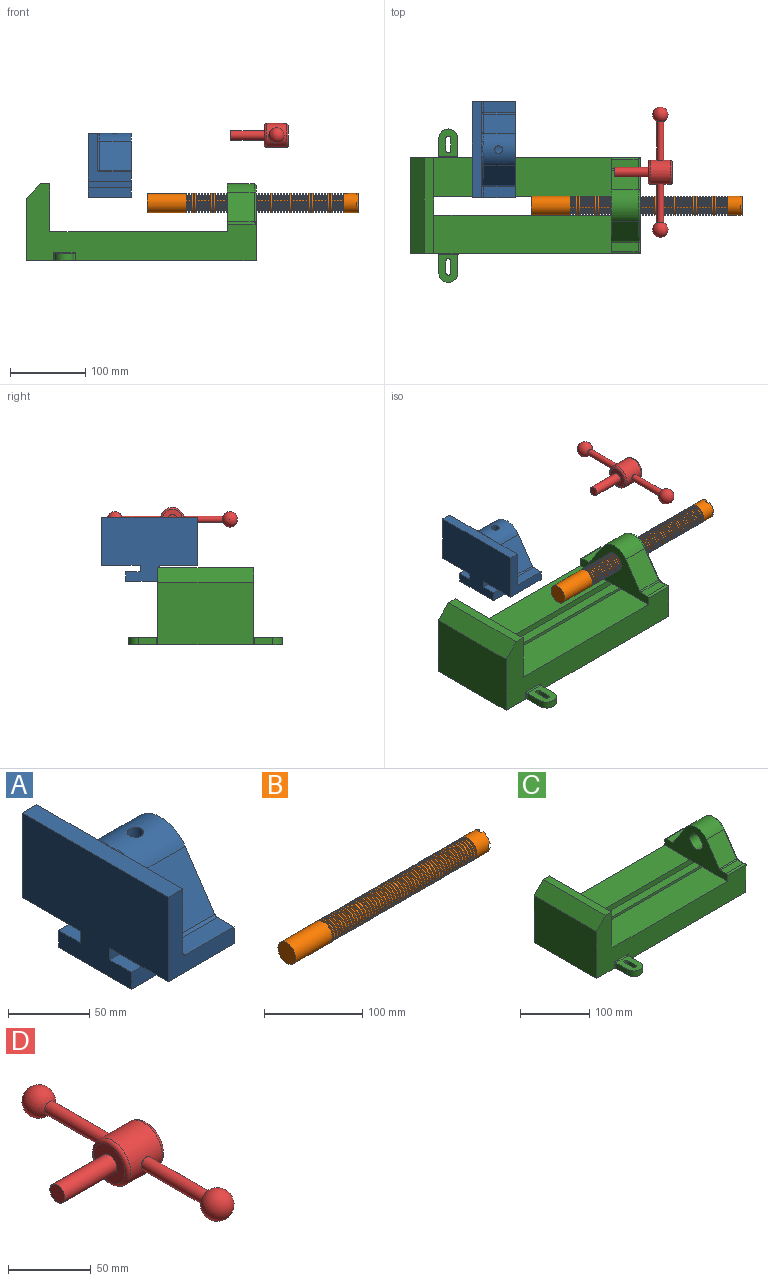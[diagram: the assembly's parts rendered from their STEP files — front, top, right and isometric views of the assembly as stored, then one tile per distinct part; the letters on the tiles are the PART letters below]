
ASSEMBLY  parts=4 mates=1
PART A: 36 faces, bbox 57.2x127x89 mm
  f0: plane 57.15x50.8mm, normal (0,0,-1), area 2903.2mm2, adj f6,f9,f10,f23
  f1: cylinder r=12.7mm len=44.45mm, axis (1,0,0), area 3464.3mm2, adj f6,f15,f16
  f2: plane 41.91x14.52mm, normal (0,0,1), area 608.5mm2, adj f6,f11,f24,f25
  f3: plane 51.86x48.26mm, normal (1,0,0), area 1495.7mm2, adj f8,f10,f31,f33,f35
  f4: plane 51.86x48.26mm, normal (1,0,0), area 1495.7mm2, adj f8,f11,f24,f28,f29
  f5: plane 57.15x50.8mm, normal (0,0,-1), area 2903.2mm2, adj f6,f9,f11,f22
  f6: plane 127x85.09mm, normal (1,0,0), area 5190.6mm2, adj f0,f1,f2,f5,f7,f10,f11,f12
  f7: plane 41.91x14.52mm, normal (0,0,1), area 608.5mm2, adj f6,f10,f30,f31
  f8: plane 127x12.7mm, normal (0,0,1), area 1612.9mm2, adj f3,f4,f9,f10,f11,f26,f34
  f9: plane 127x85.09mm, normal (-1,0,0), area 9096.8mm2, adj f0,f5,f8,f10,f11,f17,f18,f19
  f10: plane 63.5x57.15mm, normal (0,-1,0), area 1372.3mm2, adj f0,f3,f6,f7,f8,f9,f31
  f11: plane 63.5x57.15mm, normal (0,1,0), area 1372.3mm2, adj f2,f4,f5,f6,f8,f9,f24
  f12: plane 41.91x38.43mm, normal (0,-0.83,0.56), area 1939.2mm2, adj f6,f13,f30,f33
  f13: cylinder r=25.4mm len=44.45mm, axis (1,0,0), area 2026.5mm2, adj f6,f12,f14,f16,f26,f28,f34,f35
  f14: plane 41.91x38.43mm, normal (0,0.83,0.56), area 1939.2mm2, adj f6,f13,f25,f29
  f15: plane 25.4x25.4mm, normal (1,0,0), area 506.7mm2, adj f1
  f16: cylinder r=5.08mm len=13.76mm, axis (0,0,1), area 414mm2, adj f1,f13
  f17: plane 57.15x19.05mm, normal (0,0,1), area 1088.7mm2, adj f6,f9,f18,f23
  f18: plane 57.15x12.7mm, normal (0,-1,0), area 725.8mm2, adj f6,f9,f17,f19
  f19: plane 63.5x57.15mm, normal (0,0,-1), area 3629mm2, adj f6,f9,f18,f20
  f20: plane 57.15x12.7mm, normal (0,1,0), area 725.8mm2, adj f6,f9,f19,f21
  f21: plane 57.15x19.05mm, normal (0,0,1), area 1088.7mm2, adj f6,f9,f20,f22
  f22: plane 57.15x8.89mm, normal (0,1,0), area 508.1mm2, adj f5,f6,f9,f21
  f23: plane 57.15x8.89mm, normal (0,-1,0), area 508.1mm2, adj f0,f6,f9,f17
  f24: cylinder r=2.54mm len=14.52mm, axis (0,-1,0), area 57.9mm2, adj f2,f4,f11,f27
  f25: cylinder r=2.54mm len=41.91mm, axis (1,0,0), area 104.3mm2, adj f2,f6,f14,f27
  f26: bspline ~12.24x2.8mm, area 20.9mm2, adj f8,f13,f28
  f27: sphere r=2.54mm, area 6.3mm2, adj f24,f25,f29
  f28: torus R=27.94mm, axis (1,0,0), area 57.8mm2, adj f4,f13,f26,f29
  f29: cylinder r=2.54mm len=39.84mm, axis (0,-0.56,0.83), area 184.6mm2, adj f4,f14,f27,f28
  f30: cylinder r=2.54mm len=41.91mm, axis (1,0,0), area 104.3mm2, adj f6,f7,f12,f32
  f31: cylinder r=2.54mm len=14.52mm, axis (0,-1,0), area 57.9mm2, adj f3,f7,f10,f32
  f32: sphere r=2.54mm, area 6.3mm2, adj f30,f31,f33
  f33: cylinder r=2.54mm len=39.84mm, axis (0,-0.56,-0.83), area 184.6mm2, adj f3,f12,f32,f35
  f34: bspline ~12.24x2.8mm, area 20.9mm2, adj f8,f13,f35
  f35: torus R=27.94mm, axis (1,0,0), area 57.8mm2, adj f3,f13,f33,f34
PART B: 220 faces, bbox 279.4x25.4x25.4 mm
  f0: cylinder r=12.7mm len=25.4mm, axis (-1,0,0), area 1468.2mm2, adj f1,f2,f3,f5,f7,f208,f209,f210
  f1: plane 9.9x9.9mm, normal (1,0,0), area 62.3mm2, adj f0,f4,f213,f216
  f2: plane 9.9x9.9mm, normal (1,0,0), area 62.3mm2, adj f0,f4,f210,f218
  f3: plane 9.9x9.9mm, normal (1,0,0), area 62.3mm2, adj f0,f4,f209,f212
  f4: cylinder r=6.35mm len=25.4mm, axis (1,0,0), area 960.3mm2, adj f1,f2,f3,f5,f6,f208,f209,f210
  f5: plane 9.9x9.9mm, normal (1,0,0), area 62.3mm2, adj f0,f4,f215,f217
  f6: plane 12.7x12.7mm, normal (1,0,0), area 126.7mm2, adj f4
  f7: cone r=12.7mm half-angle=76deg, axis (1,0,0), area 188mm2, adj f0,f9
  f8: cone r=10.16mm half-angle=76deg, axis (-1,0,0), area 188mm2, adj f9,f10
  f9: cylinder r=10.16mm len=20.32mm, axis (1,0,0), area 81.1mm2, adj f7,f8
  f10: cylinder r=12.7mm len=25.4mm, axis (-1,0,0), area 131.7mm2, adj f8,f11
  f11: cone r=12.7mm half-angle=76deg, axis (1,0,0), area 188mm2, adj f10,f13
  f12: cone r=10.16mm half-angle=76deg, axis (-1,0,0), area 188mm2, adj f13,f14
  f13: cylinder r=10.16mm len=20.32mm, axis (1,0,0), area 81.1mm2, adj f11,f12
  f14: cylinder r=12.7mm len=25.4mm, axis (-1,0,0), area 131.7mm2, adj f12,f15
  f15: cone r=12.7mm half-angle=76deg, axis (1,0,0), area 188mm2, adj f14,f17
  f16: cone r=10.16mm half-angle=76deg, axis (-1,0,0), area 188mm2, adj f17,f18
  f17: cylinder r=10.16mm len=20.32mm, axis (1,0,0), area 81.1mm2, adj f15,f16
  f18: cylinder r=12.7mm len=25.4mm, axis (-1,0,0), area 131.7mm2, adj f16,f19
  f19: cone r=12.7mm half-angle=76deg, axis (1,0,0), area 188mm2, adj f18,f21
  f20: cone r=10.16mm half-angle=76deg, axis (-1,0,0), area 188mm2, adj f21,f22
  f21: cylinder r=10.16mm len=20.32mm, axis (1,0,0), area 81.1mm2, adj f19,f20
  f22: cylinder r=12.7mm len=25.4mm, axis (-1,0,0), area 131.7mm2, adj f20,f23
  f23: cone r=12.7mm half-angle=76deg, axis (1,0,0), area 188mm2, adj f22,f25
  f24: cone r=10.16mm half-angle=76deg, axis (-1,0,0), area 188mm2, adj f25,f26
  f25: cylinder r=10.16mm len=20.32mm, axis (1,0,0), area 81.1mm2, adj f23,f24
  f26: cylinder r=12.7mm len=25.4mm, axis (-1,0,0), area 131.7mm2, adj f24,f27
  f27: cone r=12.7mm half-angle=76deg, axis (1,0,0), area 188mm2, adj f26,f29
  f28: cone r=10.16mm half-angle=76deg, axis (-1,0,0), area 188mm2, adj f29,f30
  f29: cylinder r=10.16mm len=20.32mm, axis (1,0,0), area 81.1mm2, adj f27,f28
  f30: cylinder r=12.7mm len=25.4mm, axis (-1,0,0), area 131.7mm2, adj f28,f31
  f31: cone r=12.7mm half-angle=76deg, axis (1,0,0), area 188mm2, adj f30,f33
  f32: cone r=10.16mm half-angle=76deg, axis (-1,0,0), area 188mm2, adj f33,f34
  f33: cylinder r=10.16mm len=20.32mm, axis (1,0,0), area 81.1mm2, adj f31,f32
  f34: cylinder r=12.7mm len=25.4mm, axis (-1,0,0), area 131.7mm2, adj f32,f35
  f35: cone r=12.7mm half-angle=76deg, axis (1,0,0), area 188mm2, adj f34,f37
  f36: cone r=10.16mm half-angle=76deg, axis (-1,0,0), area 188mm2, adj f37,f38
  f37: cylinder r=10.16mm len=20.32mm, axis (1,0,0), area 81.1mm2, adj f35,f36
  f38: cylinder r=12.7mm len=25.4mm, axis (-1,0,0), area 131.7mm2, adj f36,f39
  f39: cone r=12.7mm half-angle=76deg, axis (1,0,0), area 188mm2, adj f38,f41
  f40: cone r=10.16mm half-angle=76deg, axis (-1,0,0), area 188mm2, adj f41,f42
  f41: cylinder r=10.16mm len=20.32mm, axis (1,0,0), area 81.1mm2, adj f39,f40
  f42: cylinder r=12.7mm len=25.4mm, axis (-1,0,0), area 131.7mm2, adj f40,f43
  f43: cone r=12.7mm half-angle=76deg, axis (1,0,0), area 188mm2, adj f42,f45
  f44: cone r=10.16mm half-angle=76deg, axis (-1,0,0), area 188mm2, adj f45,f46
  f45: cylinder r=10.16mm len=20.32mm, axis (1,0,0), area 81.1mm2, adj f43,f44
  f46: cylinder r=12.7mm len=25.4mm, axis (-1,0,0), area 131.7mm2, adj f44,f47
  f47: cone r=12.7mm half-angle=76deg, axis (1,0,0), area 188mm2, adj f46,f49
  f48: cone r=10.16mm half-angle=76deg, axis (-1,0,0), area 188mm2, adj f49,f50
  f49: cylinder r=10.16mm len=20.32mm, axis (1,0,0), area 81.1mm2, adj f47,f48
  f50: cylinder r=12.7mm len=25.4mm, axis (-1,0,0), area 131.7mm2, adj f48,f51
  f51: cone r=12.7mm half-angle=76deg, axis (1,0,0), area 188mm2, adj f50,f53
  f52: cone r=10.16mm half-angle=76deg, axis (-1,0,0), area 188mm2, adj f53,f54
  f53: cylinder r=10.16mm len=20.32mm, axis (1,0,0), area 81.1mm2, adj f51,f52
  f54: cylinder r=12.7mm len=25.4mm, axis (-1,0,0), area 131.7mm2, adj f52,f55
  f55: cone r=12.7mm half-angle=76deg, axis (1,0,0), area 188mm2, adj f54,f57
  f56: cone r=10.16mm half-angle=76deg, axis (-1,0,0), area 188mm2, adj f57,f58
  f57: cylinder r=10.16mm len=20.32mm, axis (1,0,0), area 81.1mm2, adj f55,f56
  f58: cylinder r=12.7mm len=25.4mm, axis (-1,0,0), area 131.7mm2, adj f56,f59
  f59: cone r=12.7mm half-angle=76deg, axis (1,0,0), area 188mm2, adj f58,f61
  f60: cone r=10.16mm half-angle=76deg, axis (-1,0,0), area 188mm2, adj f61,f62
  f61: cylinder r=10.16mm len=20.32mm, axis (1,0,0), area 81.1mm2, adj f59,f60
  f62: cylinder r=12.7mm len=25.4mm, axis (-1,0,0), area 131.7mm2, adj f60,f63
  f63: cone r=12.7mm half-angle=76deg, axis (1,0,0), area 188mm2, adj f62,f65
  f64: cone r=10.16mm half-angle=76deg, axis (-1,0,0), area 188mm2, adj f65,f66
  f65: cylinder r=10.16mm len=20.32mm, axis (1,0,0), area 81.1mm2, adj f63,f64
  f66: cylinder r=12.7mm len=25.4mm, axis (-1,0,0), area 131.7mm2, adj f64,f67
  f67: cone r=12.7mm half-angle=76deg, axis (1,0,0), area 188mm2, adj f66,f69
  f68: cone r=10.16mm half-angle=76deg, axis (-1,0,0), area 188mm2, adj f69,f70
  f69: cylinder r=10.16mm len=20.32mm, axis (1,0,0), area 81.1mm2, adj f67,f68
  f70: cylinder r=12.7mm len=25.4mm, axis (-1,0,0), area 131.7mm2, adj f68,f71
  f71: cone r=12.7mm half-angle=76deg, axis (1,0,0), area 188mm2, adj f70,f73
  f72: cone r=10.16mm half-angle=76deg, axis (-1,0,0), area 188mm2, adj f73,f74
  f73: cylinder r=10.16mm len=20.32mm, axis (1,0,0), area 81.1mm2, adj f71,f72
  f74: cylinder r=12.7mm len=25.4mm, axis (-1,0,0), area 131.7mm2, adj f72,f75
  f75: cone r=12.7mm half-angle=76deg, axis (1,0,0), area 188mm2, adj f74,f77
  f76: cone r=10.16mm half-angle=76deg, axis (-1,0,0), area 188mm2, adj f77,f78
  f77: cylinder r=10.16mm len=20.32mm, axis (1,0,0), area 81.1mm2, adj f75,f76
  f78: cylinder r=12.7mm len=25.4mm, axis (-1,0,0), area 131.7mm2, adj f76,f79
  f79: cone r=12.7mm half-angle=76deg, axis (1,0,0), area 188mm2, adj f78,f81
  f80: cone r=10.16mm half-angle=76deg, axis (-1,0,0), area 188mm2, adj f81,f82
  f81: cylinder r=10.16mm len=20.32mm, axis (1,0,0), area 81.1mm2, adj f79,f80
  f82: cylinder r=12.7mm len=25.4mm, axis (-1,0,0), area 131.7mm2, adj f80,f83
  f83: cone r=12.7mm half-angle=76deg, axis (1,0,0), area 188mm2, adj f82,f85
  f84: cone r=10.16mm half-angle=76deg, axis (-1,0,0), area 188mm2, adj f85,f86
  f85: cylinder r=10.16mm len=20.32mm, axis (1,0,0), area 81.1mm2, adj f83,f84
  f86: cylinder r=12.7mm len=25.4mm, axis (-1,0,0), area 131.7mm2, adj f84,f87
  f87: cone r=12.7mm half-angle=76deg, axis (1,0,0), area 188mm2, adj f86,f89
  f88: cone r=10.16mm half-angle=76deg, axis (-1,0,0), area 188mm2, adj f89,f90
  f89: cylinder r=10.16mm len=20.32mm, axis (1,0,0), area 81.1mm2, adj f87,f88
  f90: cylinder r=12.7mm len=25.4mm, axis (-1,0,0), area 131.7mm2, adj f88,f91
  f91: cone r=12.7mm half-angle=76deg, axis (1,0,0), area 188mm2, adj f90,f93
  f92: cone r=10.16mm half-angle=76deg, axis (-1,0,0), area 188mm2, adj f93,f94
  f93: cylinder r=10.16mm len=20.32mm, axis (1,0,0), area 81.1mm2, adj f91,f92
  f94: cylinder r=12.7mm len=25.4mm, axis (-1,0,0), area 131.7mm2, adj f92,f95
  f95: cone r=12.7mm half-angle=76deg, axis (1,0,0), area 188mm2, adj f94,f97
  f96: cone r=10.16mm half-angle=76deg, axis (-1,0,0), area 188mm2, adj f97,f98
  f97: cylinder r=10.16mm len=20.32mm, axis (1,0,0), area 81.1mm2, adj f95,f96
  f98: cylinder r=12.7mm len=25.4mm, axis (-1,0,0), area 131.7mm2, adj f96,f99
  f99: cone r=12.7mm half-angle=76deg, axis (1,0,0), area 188mm2, adj f98,f101
  f100: cone r=10.16mm half-angle=76deg, axis (-1,0,0), area 188mm2, adj f101,f102
  f101: cylinder r=10.16mm len=20.32mm, axis (1,0,0), area 81.1mm2, adj f99,f100
  f102: cylinder r=12.7mm len=25.4mm, axis (-1,0,0), area 131.7mm2, adj f100,f103
  f103: cone r=12.7mm half-angle=76deg, axis (1,0,0), area 188mm2, adj f102,f105
  f104: cone r=10.16mm half-angle=76deg, axis (-1,0,0), area 188mm2, adj f105,f106
  f105: cylinder r=10.16mm len=20.32mm, axis (1,0,0), area 81.1mm2, adj f103,f104
  f106: cylinder r=12.7mm len=25.4mm, axis (-1,0,0), area 131.7mm2, adj f104,f107
  f107: cone r=12.7mm half-angle=76deg, axis (1,0,0), area 188mm2, adj f106,f109
  f108: cone r=10.16mm half-angle=76deg, axis (-1,0,0), area 188mm2, adj f109,f110
  f109: cylinder r=10.16mm len=20.32mm, axis (1,0,0), area 81.1mm2, adj f107,f108
  f110: cylinder r=12.7mm len=25.4mm, axis (-1,0,0), area 131.7mm2, adj f108,f111
  f111: cone r=12.7mm half-angle=76deg, axis (1,0,0), area 188mm2, adj f110,f113
  f112: cone r=10.16mm half-angle=76deg, axis (-1,0,0), area 188mm2, adj f113,f114
  f113: cylinder r=10.16mm len=20.32mm, axis (1,0,0), area 81.1mm2, adj f111,f112
  f114: cylinder r=12.7mm len=25.4mm, axis (-1,0,0), area 131.7mm2, adj f112,f115
  f115: cone r=12.7mm half-angle=76deg, axis (1,0,0), area 188mm2, adj f114,f117
  f116: cone r=10.16mm half-angle=76deg, axis (-1,0,0), area 188mm2, adj f117,f118
  f117: cylinder r=10.16mm len=20.32mm, axis (1,0,0), area 81.1mm2, adj f115,f116
  f118: cylinder r=12.7mm len=25.4mm, axis (-1,0,0), area 131.7mm2, adj f116,f119
  f119: cone r=12.7mm half-angle=76deg, axis (1,0,0), area 188mm2, adj f118,f121
  f120: cone r=10.16mm half-angle=76deg, axis (-1,0,0), area 188mm2, adj f121,f122
  f121: cylinder r=10.16mm len=20.32mm, axis (1,0,0), area 81.1mm2, adj f119,f120
  f122: cylinder r=12.7mm len=25.4mm, axis (-1,0,0), area 131.7mm2, adj f120,f123
  f123: cone r=12.7mm half-angle=76deg, axis (1,0,0), area 188mm2, adj f122,f125
  f124: cone r=10.16mm half-angle=76deg, axis (-1,0,0), area 188mm2, adj f125,f126
  f125: cylinder r=10.16mm len=20.32mm, axis (1,0,0), area 81.1mm2, adj f123,f124
  f126: cylinder r=12.7mm len=25.4mm, axis (-1,0,0), area 131.7mm2, adj f124,f127
  f127: cone r=12.7mm half-angle=76deg, axis (1,0,0), area 188mm2, adj f126,f129
  f128: cone r=10.16mm half-angle=76deg, axis (-1,0,0), area 188mm2, adj f129,f130
  f129: cylinder r=10.16mm len=20.32mm, axis (1,0,0), area 81.1mm2, adj f127,f128
  f130: cylinder r=12.7mm len=25.4mm, axis (-1,0,0), area 131.7mm2, adj f128,f131
  f131: cone r=12.7mm half-angle=76deg, axis (1,0,0), area 188mm2, adj f130,f133
  f132: cone r=10.16mm half-angle=76deg, axis (-1,0,0), area 188mm2, adj f133,f134
  f133: cylinder r=10.16mm len=20.32mm, axis (1,0,0), area 81.1mm2, adj f131,f132
  f134: cylinder r=12.7mm len=25.4mm, axis (-1,0,0), area 131.7mm2, adj f132,f135
  f135: cone r=12.7mm half-angle=76deg, axis (1,0,0), area 188mm2, adj f134,f137
  f136: cone r=10.16mm half-angle=76deg, axis (-1,0,0), area 188mm2, adj f137,f138
  f137: cylinder r=10.16mm len=20.32mm, axis (1,0,0), area 81.1mm2, adj f135,f136
  f138: cylinder r=12.7mm len=25.4mm, axis (-1,0,0), area 131.7mm2, adj f136,f139
  f139: cone r=12.7mm half-angle=76deg, axis (1,0,0), area 188mm2, adj f138,f141
  f140: cone r=10.16mm half-angle=76deg, axis (-1,0,0), area 188mm2, adj f141,f142
  f141: cylinder r=10.16mm len=20.32mm, axis (1,0,0), area 81.1mm2, adj f139,f140
  f142: cylinder r=12.7mm len=25.4mm, axis (-1,0,0), area 131.7mm2, adj f140,f143
  f143: cone r=12.7mm half-angle=76deg, axis (1,0,0), area 188mm2, adj f142,f145
  f144: cone r=10.16mm half-angle=76deg, axis (-1,0,0), area 188mm2, adj f145,f146
  f145: cylinder r=10.16mm len=20.32mm, axis (1,0,0), area 81.1mm2, adj f143,f144
  f146: cylinder r=12.7mm len=25.4mm, axis (-1,0,0), area 131.7mm2, adj f144,f147
  f147: cone r=12.7mm half-angle=76deg, axis (1,0,0), area 188mm2, adj f146,f149
  f148: cone r=10.16mm half-angle=76deg, axis (-1,0,0), area 188mm2, adj f149,f150
  f149: cylinder r=10.16mm len=20.32mm, axis (1,0,0), area 81.1mm2, adj f147,f148
  f150: cylinder r=12.7mm len=25.4mm, axis (-1,0,0), area 131.7mm2, adj f148,f151
  f151: cone r=12.7mm half-angle=76deg, axis (1,0,0), area 188mm2, adj f150,f153
  f152: cone r=10.16mm half-angle=76deg, axis (-1,0,0), area 188mm2, adj f153,f154
  f153: cylinder r=10.16mm len=20.32mm, axis (1,0,0), area 81.1mm2, adj f151,f152
  f154: cylinder r=12.7mm len=25.4mm, axis (-1,0,0), area 131.7mm2, adj f152,f155
  f155: cone r=12.7mm half-angle=76deg, axis (1,0,0), area 188mm2, adj f154,f157
  f156: cone r=10.16mm half-angle=76deg, axis (-1,0,0), area 188mm2, adj f157,f158
  f157: cylinder r=10.16mm len=20.32mm, axis (1,0,0), area 81.1mm2, adj f155,f156
  f158: cylinder r=12.7mm len=25.4mm, axis (-1,0,0), area 131.7mm2, adj f156,f159
  f159: cone r=12.7mm half-angle=76deg, axis (1,0,0), area 188mm2, adj f158,f161
  f160: cone r=10.16mm half-angle=76deg, axis (-1,0,0), area 188mm2, adj f161,f162
  f161: cylinder r=10.16mm len=20.32mm, axis (1,0,0), area 81.1mm2, adj f159,f160
  f162: cylinder r=12.7mm len=25.4mm, axis (-1,0,0), area 131.7mm2, adj f160,f163
  f163: cone r=12.7mm half-angle=76deg, axis (1,0,0), area 188mm2, adj f162,f165
  f164: cone r=10.16mm half-angle=76deg, axis (-1,0,0), area 188mm2, adj f165,f166
  f165: cylinder r=10.16mm len=20.32mm, axis (1,0,0), area 81.1mm2, adj f163,f164
  f166: cylinder r=12.7mm len=25.4mm, axis (-1,0,0), area 131.7mm2, adj f164,f167
  f167: cone r=12.7mm half-angle=76deg, axis (1,0,0), area 188mm2, adj f166,f169
  f168: cone r=10.16mm half-angle=76deg, axis (-1,0,0), area 188mm2, adj f169,f170
  f169: cylinder r=10.16mm len=20.32mm, axis (1,0,0), area 81.1mm2, adj f167,f168
  f170: cylinder r=12.7mm len=25.4mm, axis (-1,0,0), area 131.7mm2, adj f168,f171
  f171: cone r=12.7mm half-angle=76deg, axis (1,0,0), area 188mm2, adj f170,f173
  f172: cone r=10.16mm half-angle=76deg, axis (-1,0,0), area 188mm2, adj f173,f174
  f173: cylinder r=10.16mm len=20.32mm, axis (1,0,0), area 81.1mm2, adj f171,f172
  f174: cylinder r=12.7mm len=25.4mm, axis (-1,0,0), area 131.7mm2, adj f172,f175
  f175: cone r=12.7mm half-angle=76deg, axis (1,0,0), area 188mm2, adj f174,f177
  f176: cone r=10.16mm half-angle=76deg, axis (-1,0,0), area 188mm2, adj f177,f178
  f177: cylinder r=10.16mm len=20.32mm, axis (1,0,0), area 81.1mm2, adj f175,f176
  f178: cylinder r=12.7mm len=25.4mm, axis (-1,0,0), area 131.7mm2, adj f176,f179
  f179: cone r=12.7mm half-angle=76deg, axis (1,0,0), area 188mm2, adj f178,f181
  f180: cone r=10.16mm half-angle=76deg, axis (-1,0,0), area 188mm2, adj f181,f182
  f181: cylinder r=10.16mm len=20.32mm, axis (1,0,0), area 81.1mm2, adj f179,f180
  f182: cylinder r=12.7mm len=25.4mm, axis (-1,0,0), area 131.7mm2, adj f180,f183
  f183: cone r=12.7mm half-angle=76deg, axis (1,0,0), area 188mm2, adj f182,f185
  f184: cone r=10.16mm half-angle=76deg, axis (-1,0,0), area 188mm2, adj f185,f186
  f185: cylinder r=10.16mm len=20.32mm, axis (1,0,0), area 81.1mm2, adj f183,f184
  f186: cylinder r=12.7mm len=25.4mm, axis (-1,0,0), area 131.7mm2, adj f184,f187
  f187: cone r=12.7mm half-angle=76deg, axis (1,0,0), area 188mm2, adj f186,f189
  f188: cone r=10.16mm half-angle=76deg, axis (-1,0,0), area 188mm2, adj f189,f190
  f189: cylinder r=10.16mm len=20.32mm, axis (1,0,0), area 81.1mm2, adj f187,f188
  f190: cylinder r=12.7mm len=25.4mm, axis (-1,0,0), area 131.7mm2, adj f188,f191
  f191: cone r=12.7mm half-angle=76deg, axis (1,0,0), area 188mm2, adj f190,f193
  f192: cone r=10.16mm half-angle=76deg, axis (-1,0,0), area 188mm2, adj f193,f194
  f193: cylinder r=10.16mm len=20.32mm, axis (1,0,0), area 81.1mm2, adj f191,f192
  f194: cylinder r=12.7mm len=25.4mm, axis (-1,0,0), area 131.7mm2, adj f192,f195
  f195: cone r=12.7mm half-angle=76deg, axis (1,0,0), area 188mm2, adj f194,f197
  f196: cone r=10.16mm half-angle=76deg, axis (-1,0,0), area 188mm2, adj f197,f198
  f197: cylinder r=10.16mm len=20.32mm, axis (1,0,0), area 81.1mm2, adj f195,f196
  f198: cylinder r=12.7mm len=25.4mm, axis (-1,0,0), area 131.7mm2, adj f196,f199
  f199: cone r=12.7mm half-angle=76deg, axis (1,0,0), area 188mm2, adj f198,f201
  f200: cone r=10.16mm half-angle=76deg, axis (-1,0,0), area 188mm2, adj f201,f202
  f201: cylinder r=10.16mm len=20.32mm, axis (1,0,0), area 81.1mm2, adj f199,f200
  f202: cylinder r=12.7mm len=25.4mm, axis (-1,0,0), area 131.7mm2, adj f200,f203
  f203: cone r=12.7mm half-angle=76deg, axis (1,0,0), area 188mm2, adj f202,f205
  f204: cone r=10.16mm half-angle=76deg, axis (-1,0,0), area 188mm2, adj f205,f207
  f205: cylinder r=10.16mm len=20.32mm, axis (1,0,0), area 81.1mm2, adj f203,f204
  f206: plane 25.4x25.4mm, normal (-1,0,0), area 506.7mm2, adj f207
  f207: cylinder r=12.7mm len=52.45mm, axis (-1,0,0), area 4185.4mm2, adj f204,f206
  f208: plane 6.88x5.08mm, normal (1,0,0), area 32.7mm2, adj f0,f4,f209,f210
  f209: plane 6.62x2.54mm, normal (0,-1,0), area 16.8mm2, adj f0,f3,f4,f208
  f210: plane 6.62x2.54mm, normal (0,1,0), area 16.8mm2, adj f0,f2,f4,f208
  f211: plane 6.88x5.08mm, normal (1,0,0), area 32.7mm2, adj f0,f4,f212,f213
  f212: plane 6.62x2.54mm, normal (0,0,1), area 16.8mm2, adj f0,f3,f4,f211
  f213: plane 6.62x2.54mm, normal (0,0,-1), area 16.8mm2, adj f0,f1,f4,f211
  f214: plane 6.88x5.08mm, normal (1,0,0), area 32.7mm2, adj f0,f4,f215,f216
  f215: plane 6.62x2.54mm, normal (0,1,0), area 16.8mm2, adj f0,f4,f5,f214
  f216: plane 6.62x2.54mm, normal (0,-1,0), area 16.8mm2, adj f0,f1,f4,f214
  f217: plane 6.62x2.54mm, normal (0,0,-1), area 16.8mm2, adj f0,f4,f5,f219
  f218: plane 6.62x2.54mm, normal (0,0,1), area 16.8mm2, adj f0,f2,f4,f219
  f219: plane 6.88x5.08mm, normal (1,0,0), area 32.7mm2, adj f0,f4,f217,f218
PART C: 61 faces, bbox 304.8x203.2x103.7 mm
  f0: plane 304.8x101.6mm, normal (0,1,0), area 13520.3mm2, adj f3,f4,f5,f6,f7,f8,f9,f16
  f1: plane 304.8x101.6mm, normal (0,-1,0), area 13520.3mm2, adj f2,f3,f5,f6,f7,f8,f9,f16
  f2: plane 234.95x50.8mm, normal (0,0,1), area 11935.5mm2, adj f1,f5,f16,f26
  f3: plane 127x99.06mm, normal (1,0,0), area 7097.5mm2, adj f0,f1,f9,f14,f17,f18,f19,f20
  f4: plane 234.95x50.8mm, normal (0,0,1), area 11935.5mm2, adj f0,f5,f16,f27
  f5: plane 127x101.6mm, normal (1,0,0), area 9516.1mm2, adj f0,f1,f2,f4,f6,f9,f18,f19
  f6: plane 127x12.7mm, normal (0,0,1), area 1612.9mm2, adj f0,f1,f5,f7
  f7: plane 127x19.05mm, normal (-0.71,0,0.71), area 3421.5mm2, adj f0,f1,f6,f8
  f8: plane 127x82.55mm, normal (-1,0,0), area 10483.8mm2, adj f0,f1,f7,f9
  f9: plane 304.8x203.2mm, normal (0,0,-1), area 33298.3mm2, adj f0,f1,f3,f5,f8,f21,f22,f39
  f10: plane 35.56x11.98mm, normal (0,0,1), area 426mm2, adj f16,f28,f29,f30
  f11: plane 38.43x35.56mm, normal (0,0.83,0.56), area 1645.4mm2, adj f12,f16,f29,f32
  f12: cylinder r=25.4mm len=42.19mm, axis (1,0,0), area 1770.2mm2, adj f11,f13,f16,f33
  f13: plane 38.43x35.56mm, normal (0,-0.83,0.56), area 1645.4mm2, adj f12,f16,f34,f35
  f14: cylinder r=12.7mm len=38.1mm, axis (1,0,0), area 3040.2mm2, adj f3,f16
  f15: plane 35.56x11.98mm, normal (0,0,1), area 426mm2, adj f16,f34,f36,f38
  f16: plane 127x63.5mm, normal (-1,0,0), area 4155.5mm2, adj f0,f1,f2,f4,f10,f11,f12,f13
  f17: plane 38.1x25.4mm, normal (0,0,-1), area 967.7mm2, adj f3,f16,f26,f27
  f18: plane 273.05x19.05mm, normal (0,0,-1), area 5201.6mm2, adj f3,f5,f19,f26
  f19: plane 273.05x12.7mm, normal (0,1,0), area 3467.7mm2, adj f3,f5,f18,f20
  f20: plane 273.05x19.05mm, normal (0,0,1), area 5201.6mm2, adj f3,f5,f19,f21
  f21: plane 273.05x16.51mm, normal (0,1,0), area 4508.1mm2, adj f3,f5,f9,f20
  f22: plane 273.05x16.51mm, normal (0,-1,0), area 4508.1mm2, adj f3,f5,f9,f23
  f23: plane 273.05x19.05mm, normal (0,0,1), area 5201.6mm2, adj f3,f5,f22,f24
  f24: plane 273.05x12.7mm, normal (0,-1,0), area 3467.7mm2, adj f3,f5,f23,f25
  f25: plane 273.05x19.05mm, normal (0,0,-1), area 5201.6mm2, adj f3,f5,f24,f27
  f26: plane 273.05x8.89mm, normal (0,1,0), area 2427.4mm2, adj f2,f3,f5,f17,f18
  f27: plane 273.05x8.89mm, normal (0,-1,0), area 2427.4mm2, adj f3,f4,f5,f17,f25
  f28: cylinder r=2.54mm len=38.1mm, axis (1,0,0), area 148.3mm2, adj f0,f10,f16,f30
  f29: cylinder r=2.54mm len=35.56mm, axis (-1,0,0), area 88.5mm2, adj f10,f11,f16,f31
  f30: cylinder r=2.54mm len=14.52mm, axis (0,1,0), area 54.3mm2, adj f3,f10,f28,f31
  f31: torus R=5.08mm, axis (-1,0,0), area 13.5mm2, adj f3,f29,f30,f32
  f32: cylinder r=2.54mm len=39.84mm, axis (0,0.56,-0.83), area 184.6mm2, adj f3,f11,f31,f33
  f33: torus R=22.86mm, axis (-1,0,0), area 191.4mm2, adj f3,f12,f32,f35
  f34: cylinder r=2.54mm len=35.56mm, axis (-1,0,0), area 88.5mm2, adj f13,f15,f16,f37
  f35: cylinder r=2.54mm len=39.84mm, axis (0,0.56,0.83), area 184.6mm2, adj f3,f13,f33,f37
  f36: cylinder r=2.54mm len=38.1mm, axis (-1,0,0), area 148.3mm2, adj f1,f15,f16,f38
  f37: torus R=5.08mm, axis (-1,0,0), area 13.5mm2, adj f3,f34,f35,f38
  f38: cylinder r=2.54mm len=14.52mm, axis (0,1,0), area 54.3mm2, adj f3,f15,f36,f37
  f39: plane 23.88x9.53mm, normal (-1,0,0), area 227.4mm2, adj f9,f45,f46,f60
  f40: plane 23.88x9.53mm, normal (1,0,0), area 227.4mm2, adj f9,f45,f46,f58
  f41: cylinder r=3.3mm len=9.53mm, axis (0,0,-1), area 98.8mm2, adj f9,f42,f44,f46
  f42: plane 15.62x9.53mm, normal (-1,0,0), area 148.8mm2, adj f9,f41,f43,f46
  f43: cylinder r=3.3mm len=9.53mm, axis (0,0,-1), area 98.8mm2, adj f9,f42,f44,f46
  f44: plane 15.62x9.53mm, normal (1,0,0), area 148.8mm2, adj f9,f41,f43,f46
  f45: cylinder r=12.7mm len=25.4mm, axis (0,0,-1), area 380mm2, adj f9,f39,f40,f46
  f46: plane 36.58x25.4mm, normal (0,0,1), area 722.4mm2, adj f39,f40,f41,f42,f43,f44,f45,f59
  f47: plane 23.88x9.53mm, normal (-1,0,0), area 227.4mm2, adj f9,f53,f54,f56
  f48: plane 23.88x9.53mm, normal (1,0,0), area 227.4mm2, adj f9,f53,f54,f55
  f49: cylinder r=3.3mm len=9.53mm, axis (0,0,-1), area 98.8mm2, adj f9,f50,f52,f54
  f50: plane 15.62x9.53mm, normal (-1,0,0), area 148.8mm2, adj f9,f49,f51,f54
  f51: cylinder r=3.3mm len=9.53mm, axis (0,0,-1), area 98.8mm2, adj f9,f50,f52,f54
  f52: plane 15.62x9.53mm, normal (1,0,0), area 148.8mm2, adj f9,f49,f51,f54
  f53: cylinder r=12.7mm len=25.4mm, axis (0,0,-1), area 380mm2, adj f9,f47,f48,f54
  f54: plane 36.58x25.4mm, normal (0,0,1), area 722.4mm2, adj f47,f48,f49,f50,f51,f52,f53,f57
  f55: cylinder r=1.52mm len=11.05mm, axis (0,0,-1), area 24.1mm2, adj f0,f9,f48,f57
  f56: cylinder r=1.52mm len=11.05mm, axis (0,0,1), area 24.1mm2, adj f0,f9,f47,f57
  f57: cylinder r=1.52mm len=28.45mm, axis (1,0,0), area 63.5mm2, adj f0,f54,f55,f56
  f58: cylinder r=1.52mm len=11.05mm, axis (0,0,1), area 24.1mm2, adj f1,f9,f40,f59
  f59: cylinder r=1.52mm len=28.45mm, axis (-1,0,0), area 63.5mm2, adj f1,f46,f58,f60
  f60: cylinder r=1.52mm len=11.05mm, axis (0,0,-1), area 24.1mm2, adj f1,f9,f39,f59
PART D: 11 faces, bbox 76.2x172.7x34.4 mm
  f0: sphere r=10.16mm, area 1231.8mm2, adj f1
  f1: cylinder r=4.45mm len=51.82mm, axis (0,1,0), area 1438.5mm2, adj f0,f4
  f2: sphere r=10.16mm, area 1231.8mm2, adj f3
  f3: cylinder r=4.45mm len=51.82mm, axis (0,1,0), area 1438.5mm2, adj f2,f4
  f4: cylinder r=15.88mm len=31.75mm, axis (-1,0,0), area 2534.7mm2, adj f1,f3,f9,f10
  f5: cylinder r=6.35mm len=44.45mm, axis (-1,0,0), area 1773.5mm2, adj f6,f8
  f6: plane 12.7x12.7mm, normal (-1,0,0), area 126.7mm2, adj f5
  f7: plane 26.67x26.67mm, normal (1,0,0), area 558.6mm2, adj f10
  f8: plane 26.67x26.67mm, normal (-1,0,0), area 432mm2, adj f5,f9
  f9: torus R=13.33mm, axis (1,0,0), area 374.8mm2, adj f4,f8
  f10: torus R=13.33mm, axis (1,0,0), area 374.8mm2, adj f4,f7
PLACE A t=(45.87,42.22,74.54)mm
PLACE B rot(axis=(1,0,0),11.2deg) t=(111.15,-17.1,8.78)mm
PLACE C t=(-4.84,-31.86,7.34)mm fixed
PLACE D t=(-31.95,12.22,96.94)mm
MATE cylindrical C.f12 <-> B.f7  axis (1,0,0) through (-42.94,-31.86,83.54)mm
